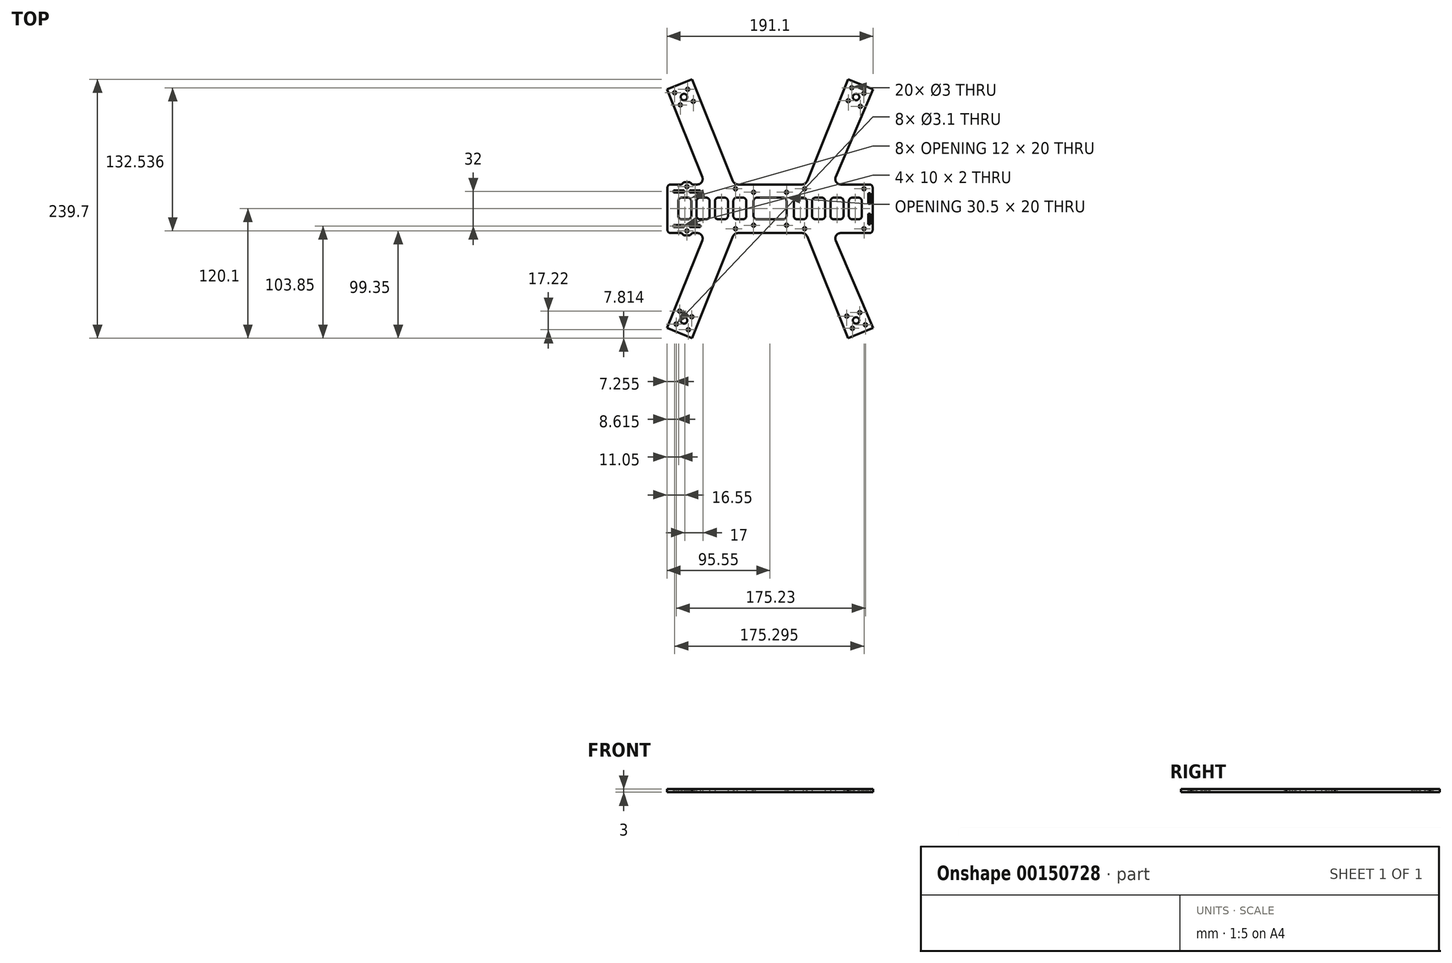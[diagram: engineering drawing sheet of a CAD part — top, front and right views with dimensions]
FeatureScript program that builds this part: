
annotation { "Feature Type Name" : "Feature", "Feature Type Description" : "" }
export const myFeature = defineFeature(function(context is Context, id is Id, definition is map)
    precondition{}
    {
        {
            var Q0;
            Q0=qCreatedBy(makeId("Top.planeOp"),FACE);
            var sketch = newSketch(context, id + "F0", { "sketchPlane" : qUnion([Q0])});
            skLineSegment(sketch, "E0.left", {"start": v(0, 42) * mm, "end": v(0, 3) * mm});
            skPoint(sketch, "E1.startSnap0", {"position": v(0, 22.5) * mm});
            skPoint(sketch, "E2.visualSharp", {"position": v(0, 45) * mm});
            skArc(sketch, "E2.filletArc", {"start": v(3, 45) * mm, "mid": v(0.88, 44.12) * mm, "end": v(0, 42) * mm});
            skPoint(sketch, "E3.visualSharp", {"position": v(0, 0) * mm});
            skArc(sketch, "E3.filletArc", {"start": v(0, 3) * mm, "mid": v(0.88, 0.88) * mm, "end": v(3, 0) * mm});
            skPoint(sketch, "E4.visualSharp", {"position": v(190, 45) * mm});
            skPoint(sketch, "E5.visualSharp", {"position": v(190, 0) * mm});
            skLineSegment(sketch, "E6", {"start": v(-0.55, -87.99) * mm, "end": v(22.63, -97.35) * mm});
            skLineSegment(sketch, "E7", {"start": v(95, 32.04) * mm, "end": v(95, 12.26) * mm, "construction": true});
            skPoint(sketch, "E7.startSnap0", {"position": v(95, 45) * mm});
            skLineSegment(sketch, "E8", {"start": v(11.04, -92.67) * mm, "end": v(15.32, -80.93) * mm, "construction": true});
            skCircle(sketch, "E9", {"center": v(15.32, -80.93) * mm, "radius": 13 * mm, "construction": true});
            skCircle(sketch, "E10", {"center": v(15.32, -80.93) * mm, "radius": 8 * mm, "construction": true});
            skCircle(sketch, "E11", {"center": v(15.32, -80.93) * mm, "radius": 9.5 * mm, "construction": true});
            skLineSegment(sketch, "E12", {"start": v(15.32, -80.93) * mm, "end": v(22.57, -77.54) * mm, "construction": true});
            skLineSegment(sketch, "E13", {"start": v(15.32, -80.93) * mm, "end": v(8.06, -84.3) * mm, "construction": true});
            skLineSegment(sketch, "E14", {"start": v(15.32, -80.93) * mm, "end": v(11.3, -72.32) * mm, "construction": true});
            skLineSegment(sketch, "E15", {"start": v(15.32, -80.93) * mm, "end": v(19.33, -89.54) * mm, "construction": true});
            skCircle(sketch, "E16", {"center": v(11.3, -72.32) * mm, "radius": 1.55 * mm});
            skCircle(sketch, "E17", {"center": v(19.33, -89.54) * mm, "radius": 1.55 * mm});
            skCircle(sketch, "E18", {"center": v(22.57, -77.54) * mm, "radius": 1.55 * mm});
            skCircle(sketch, "E19", {"center": v(8.06, -84.3) * mm, "radius": 1.55 * mm});
            skCircle(sketch, "E20", {"center": v(15.32, -80.93) * mm, "radius": 3 * mm});
            skLineSegment(sketch, "E21.MirrorCS", {"start": v(190.55, -87.99) * mm, "end": v(167.37, -97.35) * mm});
            skCircle(sketch, "E22.MirrorC", {"center": v(174.68, -80.93) * mm, "radius": 3 * mm});
            skLineSegment(sketch, "E23.MirrorCS", {"start": v(178.96, -92.67) * mm, "end": v(174.68, -80.93) * mm, "construction": true});
            skCircle(sketch, "E24.MirrorC", {"center": v(174.68, -80.93) * mm, "radius": 8 * mm, "construction": true});
            skCircle(sketch, "E25.MirrorC", {"center": v(174.68, -80.93) * mm, "radius": 9.5 * mm, "construction": true});
            skLineSegment(sketch, "E26", {"start": v(174.68, -80.93) * mm, "end": v(166.07, -76.91) * mm, "construction": true});
            skLineSegment(sketch, "E27", {"start": v(174.68, -80.93) * mm, "end": v(183.3, -84.94) * mm, "construction": true});
            skLineSegment(sketch, "E28", {"start": v(174.68, -80.93) * mm, "end": v(178.07, -73.68) * mm, "construction": true});
            skLineSegment(sketch, "E29", {"start": v(174.68, -80.93) * mm, "end": v(171.3, -88.18) * mm, "construction": true});
            skCircle(sketch, "E30", {"center": v(166.07, -76.91) * mm, "radius": 1.55 * mm});
            skCircle(sketch, "E31", {"center": v(178.07, -73.68) * mm, "radius": 1.55 * mm});
            skCircle(sketch, "E32", {"center": v(171.3, -88.18) * mm, "radius": 1.55 * mm});
            skCircle(sketch, "E33", {"center": v(183.3, -84.94) * mm, "radius": 1.55 * mm});
            skLineSegment(sketch, "E34.bottom", {"start": v(110.25, 7.25) * mm, "end": v(79.75, 7.25) * mm, "construction": true});
            skLineSegment(sketch, "E34.top", {"start": v(110.25, 37.75) * mm, "end": v(79.75, 37.75) * mm, "construction": true});
            skCircle(sketch, "E35", {"center": v(110.25, 7.25) * mm, "radius": 1.5 * mm});
            skCircle(sketch, "E36", {"center": v(79.75, 7.25) * mm, "radius": 1.5 * mm});
            skCircle(sketch, "E37", {"center": v(110.25, 37.75) * mm, "radius": 1.5 * mm});
            skCircle(sketch, "E38", {"center": v(79.75, 37.75) * mm, "radius": 1.5 * mm});
            skLineSegment(sketch, "E39.bottom", {"start": v(177, 12.75) * mm, "end": v(171, 12.75) * mm});
            skLineSegment(sketch, "E39.top", {"start": v(177, 32.75) * mm, "end": v(171, 32.75) * mm});
            skLineSegment(sketch, "E39.left", {"start": v(180, 15.75) * mm, "end": v(180, 29.75) * mm});
            skLineSegment(sketch, "E39.right", {"start": v(168, 15.75) * mm, "end": v(168, 29.75) * mm});
            skPoint(sketch, "E40.visualSharp", {"position": v(180, 12.75) * mm});
            skArc(sketch, "E40.filletArc", {"start": v(177, 12.75) * mm, "mid": v(179.12, 13.63) * mm, "end": v(180, 15.75) * mm});
            skPoint(sketch, "E41.visualSharp", {"position": v(168, 12.75) * mm});
            skArc(sketch, "E41.filletArc", {"start": v(168, 15.75) * mm, "mid": v(168.88, 13.63) * mm, "end": v(171, 12.75) * mm});
            skPoint(sketch, "E42.visualSharp", {"position": v(168, 32.75) * mm});
            skArc(sketch, "E42.filletArc", {"start": v(171, 32.75) * mm, "mid": v(168.88, 31.87) * mm, "end": v(168, 29.75) * mm});
            skPoint(sketch, "E43.visualSharp", {"position": v(180, 32.75) * mm});
            skArc(sketch, "E43.filletArc", {"start": v(180, 29.75) * mm, "mid": v(179.12, 31.87) * mm, "end": v(177, 32.75) * mm});
            skPoint(sketch, "E44.1.0.0", {"position": v(163, 12.75) * mm});
            skLineSegment(sketch, "E44.1.0.1", {"start": v(151, 15.75) * mm, "end": v(151, 29.75) * mm});
            skLineSegment(sketch, "E44.1.0.2", {"start": v(160, 32.75) * mm, "end": v(154, 32.75) * mm});
            skLineSegment(sketch, "E44.1.0.3", {"start": v(163, 15.75) * mm, "end": v(163, 29.75) * mm});
            skLineSegment(sketch, "E44.1.0.4", {"start": v(160, 12.75) * mm, "end": v(154, 12.75) * mm});
            skPoint(sketch, "E44.1.0.5", {"position": v(151, 12.75) * mm});
            skPoint(sketch, "E44.1.0.6", {"position": v(163, 32.75) * mm});
            skPoint(sketch, "E44.1.0.7", {"position": v(151, 32.75) * mm});
            skArc(sketch, "E44.1.0.8", {"start": v(160, 12.75) * mm, "mid": v(162.12, 13.63) * mm, "end": v(163, 15.75) * mm});
            skArc(sketch, "E44.1.0.9", {"start": v(154, 32.75) * mm, "mid": v(151.88, 31.87) * mm, "end": v(151, 29.75) * mm});
            skArc(sketch, "E44.1.0.10", {"start": v(151, 15.75) * mm, "mid": v(151.88, 13.63) * mm, "end": v(154, 12.75) * mm});
            skArc(sketch, "E44.1.0.11", {"start": v(163, 29.75) * mm, "mid": v(162.12, 31.87) * mm, "end": v(160, 32.75) * mm});
            skPoint(sketch, "E44.2.0.0", {"position": v(146, 12.75) * mm});
            skLineSegment(sketch, "E44.2.0.1", {"start": v(134, 15.75) * mm, "end": v(134, 29.75) * mm});
            skLineSegment(sketch, "E44.2.0.2", {"start": v(143, 32.75) * mm, "end": v(137, 32.75) * mm});
            skLineSegment(sketch, "E44.2.0.3", {"start": v(146, 15.75) * mm, "end": v(146, 29.75) * mm});
            skLineSegment(sketch, "E44.2.0.4", {"start": v(143, 12.75) * mm, "end": v(137, 12.75) * mm});
            skPoint(sketch, "E44.2.0.5", {"position": v(134, 12.75) * mm});
            skPoint(sketch, "E44.2.0.6", {"position": v(146, 32.75) * mm});
            skPoint(sketch, "E44.2.0.7", {"position": v(134, 32.75) * mm});
            skArc(sketch, "E44.2.0.8", {"start": v(143, 12.75) * mm, "mid": v(145.12, 13.63) * mm, "end": v(146, 15.75) * mm});
            skArc(sketch, "E44.2.0.9", {"start": v(137, 32.75) * mm, "mid": v(134.88, 31.87) * mm, "end": v(134, 29.75) * mm});
            skArc(sketch, "E44.2.0.10", {"start": v(134, 15.75) * mm, "mid": v(134.88, 13.63) * mm, "end": v(137, 12.75) * mm});
            skArc(sketch, "E44.2.0.11", {"start": v(146, 29.75) * mm, "mid": v(145.12, 31.87) * mm, "end": v(143, 32.75) * mm});
            skPoint(sketch, "E44.3.0.0", {"position": v(129, 12.75) * mm});
            skLineSegment(sketch, "E44.3.0.1", {"start": v(117, 15.75) * mm, "end": v(117, 29.75) * mm});
            skLineSegment(sketch, "E44.3.0.2", {"start": v(126, 32.75) * mm, "end": v(120, 32.75) * mm});
            skLineSegment(sketch, "E44.3.0.3", {"start": v(129, 15.75) * mm, "end": v(129, 29.75) * mm});
            skLineSegment(sketch, "E44.3.0.4", {"start": v(126, 12.75) * mm, "end": v(120, 12.75) * mm});
            skPoint(sketch, "E44.3.0.5", {"position": v(117, 12.75) * mm});
            skPoint(sketch, "E44.3.0.6", {"position": v(129, 32.75) * mm});
            skPoint(sketch, "E44.3.0.7", {"position": v(117, 32.75) * mm});
            skArc(sketch, "E44.3.0.8", {"start": v(126, 12.75) * mm, "mid": v(128.12, 13.63) * mm, "end": v(129, 15.75) * mm});
            skArc(sketch, "E44.3.0.9", {"start": v(120, 32.75) * mm, "mid": v(117.88, 31.87) * mm, "end": v(117, 29.75) * mm});
            skArc(sketch, "E44.3.0.10", {"start": v(117, 15.75) * mm, "mid": v(117.88, 13.63) * mm, "end": v(120, 12.75) * mm});
            skArc(sketch, "E44.3.0.11", {"start": v(129, 29.75) * mm, "mid": v(128.12, 31.87) * mm, "end": v(126, 32.75) * mm});
            skLineSegment(sketch, "E44.direction1", {"start": v(168, 12.75) * mm, "end": v(151, 12.75) * mm, "construction": true});
            skLineSegment(sketch, "E45.bottom", {"start": v(107.25, 12.75) * mm, "end": v(82.75, 12.75) * mm});
            skLineSegment(sketch, "E45.top", {"start": v(107.25, 32.75) * mm, "end": v(82.75, 32.75) * mm});
            skLineSegment(sketch, "E45.left", {"start": v(110.25, 15.75) * mm, "end": v(110.25, 29.75) * mm});
            skLineSegment(sketch, "E45.right", {"start": v(79.75, 15.75) * mm, "end": v(79.75, 29.75) * mm});
            skPoint(sketch, "E46.visualSharp", {"position": v(110.25, 12.75) * mm});
            skArc(sketch, "E46.filletArc", {"start": v(107.25, 12.75) * mm, "mid": v(109.37, 13.63) * mm, "end": v(110.25, 15.75) * mm});
            skPoint(sketch, "E47.visualSharp", {"position": v(110.25, 32.75) * mm});
            skArc(sketch, "E47.filletArc", {"start": v(110.25, 29.75) * mm, "mid": v(109.37, 31.87) * mm, "end": v(107.25, 32.75) * mm});
            skPoint(sketch, "E48.visualSharp", {"position": v(79.75, 32.75) * mm});
            skArc(sketch, "E48.filletArc", {"start": v(82.75, 32.75) * mm, "mid": v(80.63, 31.87) * mm, "end": v(79.75, 29.75) * mm});
            skPoint(sketch, "E49.visualSharp", {"position": v(79.75, 12.75) * mm});
            skArc(sketch, "E49.filletArc", {"start": v(79.75, 15.75) * mm, "mid": v(80.63, 13.63) * mm, "end": v(82.75, 12.75) * mm});
            skArc(sketch, "E50.MirrorCS", {"start": v(44, 29.75) * mm, "mid": v(44.88, 31.87) * mm, "end": v(47, 32.75) * mm});
            skArc(sketch, "E51.MirrorCS", {"start": v(61, 29.75) * mm, "mid": v(61.88, 31.87) * mm, "end": v(64, 32.75) * mm});
            skArc(sketch, "E52.MirrorCS", {"start": v(70, 32.75) * mm, "mid": v(72.12, 31.87) * mm, "end": v(73, 29.75) * mm});
            skArc(sketch, "E53.MirrorCS", {"start": v(64, 12.75) * mm, "mid": v(61.88, 13.63) * mm, "end": v(61, 15.75) * mm});
            skArc(sketch, "E54.MirrorCS", {"start": v(73, 15.75) * mm, "mid": v(72.12, 13.63) * mm, "end": v(70, 12.75) * mm});
            skArc(sketch, "E55.MirrorCS", {"start": v(53, 32.75) * mm, "mid": v(55.12, 31.87) * mm, "end": v(56, 29.75) * mm});
            skArc(sketch, "E56.MirrorCS", {"start": v(56, 15.75) * mm, "mid": v(55.12, 13.63) * mm, "end": v(53, 12.75) * mm});
            skArc(sketch, "E57.MirrorCS", {"start": v(47, 12.75) * mm, "mid": v(44.88, 13.63) * mm, "end": v(44, 15.75) * mm});
            skLineSegment(sketch, "E58.MirrorCS", {"start": v(56, 15.75) * mm, "end": v(56, 29.75) * mm});
            skPoint(sketch, "E59.MirrorP", {"position": v(44, 12.75) * mm});
            skLineSegment(sketch, "E60.MirrorCS", {"start": v(64, 32.75) * mm, "end": v(70, 32.75) * mm});
            skPoint(sketch, "E61.MirrorP", {"position": v(61, 12.75) * mm});
            skPoint(sketch, "E62.MirrorP", {"position": v(39, 12.75) * mm});
            skPoint(sketch, "E63.MirrorP", {"position": v(44, 32.75) * mm});
            skPoint(sketch, "E64.MirrorP", {"position": v(56, 12.75) * mm});
            skLineSegment(sketch, "E65.MirrorCS", {"start": v(44, 15.75) * mm, "end": v(44, 29.75) * mm});
            skLineSegment(sketch, "E66.MirrorCS", {"start": v(47, 12.75) * mm, "end": v(53, 12.75) * mm});
            skLineSegment(sketch, "E67.MirrorCS", {"start": v(73, 15.75) * mm, "end": v(73, 29.75) * mm});
            skPoint(sketch, "E68.MirrorP", {"position": v(73, 32.75) * mm});
            skPoint(sketch, "E69.MirrorP", {"position": v(61, 32.75) * mm});
            skLineSegment(sketch, "E70.MirrorCS", {"start": v(64, 12.75) * mm, "end": v(70, 12.75) * mm});
            skLineSegment(sketch, "E71.MirrorCS", {"start": v(47, 32.75) * mm, "end": v(53, 32.75) * mm});
            skPoint(sketch, "E72.MirrorP", {"position": v(73, 12.75) * mm});
            skPoint(sketch, "E73.MirrorP", {"position": v(39, 32.75) * mm});
            skPoint(sketch, "E74.MirrorP", {"position": v(56, 32.75) * mm});
            skLineSegment(sketch, "E75.MirrorCS", {"start": v(61, 15.75) * mm, "end": v(61, 29.75) * mm});
            skLineSegment(sketch, "E76.bottom", {"start": v(20.5, 39.5) * mm, "end": v(30.5, 39.5) * mm});
            skLineSegment(sketch, "E76.top", {"start": v(20.5, 37.5) * mm, "end": v(30.5, 37.5) * mm});
            skLineSegment(sketch, "E76.left", {"start": v(20.5, 39.5) * mm, "end": v(20.5, 37.5) * mm});
            skLineSegment(sketch, "E76.right", {"start": v(30.5, 39.5) * mm, "end": v(30.5, 37.5) * mm});
            skLineSegment(sketch, "E77.MirrorCS", {"start": v(30.5, 5.5) * mm, "end": v(30.5, 7.5) * mm});
            skLineSegment(sketch, "E78.MirrorCS", {"start": v(20.5, 5.5) * mm, "end": v(20.5, 7.5) * mm});
            skLineSegment(sketch, "E79.MirrorCS", {"start": v(15.5, 5.5) * mm, "end": v(15.5, 7.5) * mm});
            skLineSegment(sketch, "E80.MirrorCS", {"start": v(5.5, 5.5) * mm, "end": v(5.5, 7.5) * mm});
            skLineSegment(sketch, "E81.MirrorCS", {"start": v(20.5, 7.5) * mm, "end": v(30.5, 7.5) * mm});
            skLineSegment(sketch, "E82.MirrorCS", {"start": v(20.5, 5.5) * mm, "end": v(30.5, 5.5) * mm});
            skLineSegment(sketch, "E83.MirrorCS", {"start": v(5.5, 7.5) * mm, "end": v(15.5, 7.5) * mm});
            skLineSegment(sketch, "E84.MirrorCS", {"start": v(5.5, 5.5) * mm, "end": v(15.5, 5.5) * mm});
            skLineSegment(sketch, "E85", {"start": v(87.1, 22.5) * mm, "end": v(104.02, 22.5) * mm, "construction": true});
            skCircle(sketch, "E86", {"center": v(63, 41) * mm, "radius": 1.5 * mm});
            skCircle(sketch, "E87.MirrorC", {"center": v(63, 4) * mm, "radius": 1.5 * mm});
            skLineSegment(sketch, "E88.bottom", {"start": v(186, 37) * mm, "end": v(188, 37) * mm});
            skLineSegment(sketch, "E88.top", {"start": v(186, 27) * mm, "end": v(188, 27) * mm});
            skLineSegment(sketch, "E88.left", {"start": v(186, 37) * mm, "end": v(186, 27) * mm});
            skLineSegment(sketch, "E88.right", {"start": v(188, 37) * mm, "end": v(188, 27) * mm});
            skLineSegment(sketch, "E89.MirrorCS", {"start": v(188, 8) * mm, "end": v(188, 18) * mm});
            skLineSegment(sketch, "E90.MirrorCS", {"start": v(186, 8) * mm, "end": v(186, 18) * mm});
            skLineSegment(sketch, "E91.MirrorCS", {"start": v(186, 18) * mm, "end": v(188, 18) * mm});
            skLineSegment(sketch, "E92.MirrorCS", {"start": v(186, 8) * mm, "end": v(188, 8) * mm});
            skCircle(sketch, "E93", {"center": v(182, 41) * mm, "radius": 1.5 * mm});
            skCircle(sketch, "E94.MirrorC", {"center": v(182, 4) * mm, "radius": 1.5 * mm});
            skCircle(sketch, "E95", {"center": v(127, 41) * mm, "radius": 1.5 * mm});
            skCircle(sketch, "E96.MirrorC", {"center": v(127, 4) * mm, "radius": 1.5 * mm});
            skLineSegment(sketch, "E97.MirrorCS", {"start": v(5.5, 39.5) * mm, "end": v(5.5, 37.5) * mm});
            skLineSegment(sketch, "E98.MirrorCS", {"start": v(15.5, 39.5) * mm, "end": v(15.5, 37.5) * mm});
            skLineSegment(sketch, "E99.MirrorCS", {"start": v(5.5, 37.5) * mm, "end": v(15.5, 37.5) * mm});
            skLineSegment(sketch, "E100.MirrorCS", {"start": v(5.5, 39.5) * mm, "end": v(15.5, 39.5) * mm});
            skLineSegment(sketch, "E101", {"start": v(13, 45) * mm, "end": v(14.7, 46.7) * mm});
            skLineSegment(sketch, "E102", {"start": v(15.41, 47) * mm, "end": v(20.59, 47) * mm});
            skLineSegment(sketch, "E103", {"start": v(21.3, 46.7) * mm, "end": v(23, 45) * mm});
            skPoint(sketch, "E104.visualSharp", {"position": v(15, 47) * mm});
            skArc(sketch, "E104.filletArc", {"start": v(15.41, 47) * mm, "mid": v(15.03, 46.92) * mm, "end": v(14.7, 46.7) * mm});
            skPoint(sketch, "E105.visualSharp", {"position": v(21, 47) * mm});
            skArc(sketch, "E105.filletArc", {"start": v(21.3, 46.7) * mm, "mid": v(20.97, 46.92) * mm, "end": v(20.59, 47) * mm});
            skArc(sketch, "E106.MirrorCS", {"start": v(39, 15.75) * mm, "mid": v(38.12, 13.63) * mm, "end": v(36, 12.75) * mm});
            skArc(sketch, "E107.MirrorCS", {"start": v(22, 15.75) * mm, "mid": v(21.12, 13.63) * mm, "end": v(19, 12.75) * mm});
            skArc(sketch, "E108.MirrorCS", {"start": v(36, 32.75) * mm, "mid": v(38.12, 31.87) * mm, "end": v(39, 29.75) * mm});
            skArc(sketch, "E109.MirrorCS", {"start": v(30, 12.75) * mm, "mid": v(27.88, 13.63) * mm, "end": v(27, 15.75) * mm});
            skLineSegment(sketch, "E110.MirrorCS", {"start": v(30, 12.75) * mm, "end": v(36, 12.75) * mm});
            skArc(sketch, "E111.MirrorCS", {"start": v(10, 29.75) * mm, "mid": v(10.88, 31.87) * mm, "end": v(13, 32.75) * mm});
            skArc(sketch, "E112.MirrorCS", {"start": v(19, 32.75) * mm, "mid": v(21.12, 31.87) * mm, "end": v(22, 29.75) * mm});
            skArc(sketch, "E113.MirrorCS", {"start": v(13, 12.75) * mm, "mid": v(10.88, 13.63) * mm, "end": v(10, 15.75) * mm});
            skArc(sketch, "E114.MirrorCS", {"start": v(27, 29.75) * mm, "mid": v(27.88, 31.87) * mm, "end": v(30, 32.75) * mm});
            skPoint(sketch, "E115.MirrorP", {"position": v(27, 12.75) * mm});
            skPoint(sketch, "E116.MirrorP", {"position": v(10, 32.75) * mm});
            skLineSegment(sketch, "E117.MirrorCS", {"start": v(30, 32.75) * mm, "end": v(36, 32.75) * mm});
            skPoint(sketch, "E118.MirrorP", {"position": v(22, 12.75) * mm});
            skLineSegment(sketch, "E119.MirrorCS", {"start": v(27, 15.75) * mm, "end": v(27, 29.75) * mm});
            skPoint(sketch, "E120.MirrorP", {"position": v(22, 32.75) * mm});
            skLineSegment(sketch, "E121.MirrorCS", {"start": v(39, 15.75) * mm, "end": v(39, 29.75) * mm});
            skPoint(sketch, "E122.MirrorP", {"position": v(10, 12.75) * mm});
            skPoint(sketch, "E123.MirrorP", {"position": v(27, 32.75) * mm});
            skLineSegment(sketch, "E124.MirrorCS", {"start": v(22, 15.75) * mm, "end": v(22, 29.75) * mm});
            skLineSegment(sketch, "E125.MirrorCS", {"start": v(10, 15.75) * mm, "end": v(10, 29.75) * mm});
            skLineSegment(sketch, "E126.MirrorCS", {"start": v(13, 32.75) * mm, "end": v(19, 32.75) * mm});
            skLineSegment(sketch, "E127.MirrorCS", {"start": v(22, 12.75) * mm, "end": v(39, 12.75) * mm, "construction": true});
            skLineSegment(sketch, "E128.MirrorCS", {"start": v(13, 12.75) * mm, "end": v(19, 12.75) * mm});
            skCircle(sketch, "E129", {"center": v(18, 43) * mm, "radius": 1.5 * mm});
            skCircle(sketch, "E130.MirrorC", {"center": v(18, 2) * mm, "radius": 1.5 * mm});
            skArc(sketch, "E131.MirrorCS", {"start": v(21.3, -1.7) * mm, "mid": v(20.97, -1.92) * mm, "end": v(20.59, -2) * mm});
            skArc(sketch, "E132.MirrorCS", {"start": v(15.41, -2) * mm, "mid": v(15.03, -1.92) * mm, "end": v(14.7, -1.7) * mm});
            skPoint(sketch, "E133.MirrorP", {"position": v(21, -2) * mm});
            skLineSegment(sketch, "E134.MirrorCS", {"start": v(15.41, -2) * mm, "end": v(20.59, -2) * mm});
            skPoint(sketch, "E135.MirrorP", {"position": v(15, -2) * mm});
            skLineSegment(sketch, "E136.MirrorCS", {"start": v(13, 0) * mm, "end": v(14.7, -1.7) * mm});
            skLineSegment(sketch, "E137.MirrorCS", {"start": v(21.3, -1.7) * mm, "end": v(23, 0) * mm});
            skCircle(sketch, "E138", {"center": v(15.32, -80.93) * mm, "radius": 77 * mm, "construction": true});
            skLineSegment(sketch, "E139", {"start": v(13, 0) * mm, "end": v(3, 0) * mm});
            skCircle(sketch, "E140.MirrorC", {"center": v(174.68, -80.93) * mm, "radius": 77 * mm, "construction": true});
            skPoint(sketch, "E141.visualSharp", {"position": v(61.96, 0) * mm});
            skLineSegment(sketch, "E142.MirrorCS", {"start": v(167.37, -97.35) * mm, "end": v(129.3, -3.13) * mm});
            skLineSegment(sketch, "E143.MirrorCS", {"start": v(190.55, -87.99) * mm, "end": v(155.83, -6.97) * mm});
            skLineSegment(sketch, "E144", {"start": v(65.34, 0) * mm, "end": v(124.66, 0) * mm});
            skPoint(sketch, "E145.visualSharp", {"position": v(128.04, 0) * mm});
            skArc(sketch, "E145.filletArc", {"start": v(129.3, -3.13) * mm, "mid": v(127.46, -0.85) * mm, "end": v(124.66, 0) * mm});
            skPoint(sketch, "E146.visualSharp", {"position": v(152.85, 0) * mm});
            skArc(sketch, "E146.filletArc", {"start": v(160.43, 0) * mm, "mid": v(156.26, -2.25) * mm, "end": v(155.83, -6.97) * mm});
            skLineSegment(sketch, "E147.MirrorCS", {"start": v(13, 45) * mm, "end": v(3, 45) * mm});
            skCircle(sketch, "E148.MirrorC", {"center": v(15.32, 125.93) * mm, "radius": 77 * mm, "construction": true});
            skArc(sketch, "E149.MirrorCS", {"start": v(129.3, 48.13) * mm, "mid": v(127.46, 45.85) * mm, "end": v(124.66, 45) * mm});
            skLineSegment(sketch, "E150.MirrorCS", {"start": v(190.55, 132.99) * mm, "end": v(155.83, 51.97) * mm});
            skLineSegment(sketch, "E151.MirrorCS", {"start": v(190.55, 132.99) * mm, "end": v(167.37, 142.35) * mm});
            skCircle(sketch, "E152.MirrorC", {"center": v(174.68, 125.93) * mm, "radius": 77 * mm, "construction": true});
            skLineSegment(sketch, "E153.MirrorCS", {"start": v(-0.55, 132.99) * mm, "end": v(22.63, 142.35) * mm});
            skCircle(sketch, "E154.MirrorC", {"center": v(15.32, 125.93) * mm, "radius": 9.5 * mm, "construction": true});
            skCircle(sketch, "E155.MirrorC", {"center": v(15.32, 125.93) * mm, "radius": 8 * mm, "construction": true});
            skCircle(sketch, "E156.MirrorC", {"center": v(15.32, 125.93) * mm, "radius": 3 * mm});
            skCircle(sketch, "E157.MirrorC", {"center": v(174.68, 125.93) * mm, "radius": 3 * mm});
            skCircle(sketch, "E158.MirrorC", {"center": v(174.68, 125.93) * mm, "radius": 8 * mm, "construction": true});
            skCircle(sketch, "E159.MirrorC", {"center": v(174.68, 125.93) * mm, "radius": 9.5 * mm, "construction": true});
            skLineSegment(sketch, "E160", {"start": v(174.68, 125.93) * mm, "end": v(167.43, 122.54) * mm, "construction": true});
            skLineSegment(sketch, "E161", {"start": v(174.68, 125.93) * mm, "end": v(170.67, 134.54) * mm, "construction": true});
            skLineSegment(sketch, "E162", {"start": v(174.68, 125.93) * mm, "end": v(178.7, 117.32) * mm, "construction": true});
            skLineSegment(sketch, "E163", {"start": v(174.68, 125.93) * mm, "end": v(181.94, 129.3) * mm});
            skLineSegment(sketch, "E164", {"start": v(15.32, 125.93) * mm, "end": v(6.7, 129.94) * mm, "construction": true});
            skLineSegment(sketch, "E165", {"start": v(15.32, 125.93) * mm, "end": v(23.93, 121.91) * mm, "construction": true});
            skLineSegment(sketch, "E166", {"start": v(15.32, 125.93) * mm, "end": v(11.93, 118.68) * mm, "construction": true});
            skLineSegment(sketch, "E167", {"start": v(15.32, 125.93) * mm, "end": v(18.7, 133.18) * mm, "construction": true});
            skCircle(sketch, "E168", {"center": v(6.7, 129.94) * mm, "radius": 1.5 * mm});
            skCircle(sketch, "E169", {"center": v(18.7, 133.18) * mm, "radius": 1.5 * mm});
            skCircle(sketch, "E170", {"center": v(23.93, 121.91) * mm, "radius": 1.5 * mm});
            skCircle(sketch, "E171", {"center": v(11.93, 118.68) * mm, "radius": 1.5 * mm});
            skCircle(sketch, "E172", {"center": v(170.67, 134.54) * mm, "radius": 1.5 * mm});
            skCircle(sketch, "E173", {"center": v(181.94, 129.3) * mm, "radius": 1.5 * mm});
            skCircle(sketch, "E174", {"center": v(178.7, 117.32) * mm, "radius": 1.5 * mm});
            skCircle(sketch, "E175", {"center": v(167.43, 122.54) * mm, "radius": 1.5 * mm});
            skLineSegment(sketch, "E176", {"start": v(22.63, -97.35) * mm, "end": v(60.7, -3.13) * mm});
            skLineSegment(sketch, "E177", {"start": v(-0.55, -87.99) * mm, "end": v(32.22, -6.87) * mm});
            skLineSegment(sketch, "E178", {"start": v(23, 0) * mm, "end": v(27.59, 0) * mm});
            skLineSegment(sketch, "E179.MirrorCS", {"start": v(23, 45) * mm, "end": v(27.59, 45) * mm});
            skLineSegment(sketch, "E180.MirrorCS", {"start": v(-0.55, 132.99) * mm, "end": v(32.22, 51.87) * mm});
            skLineSegment(sketch, "E181.MirrorCS", {"start": v(22.63, 142.35) * mm, "end": v(60.7, 48.13) * mm});
            skLineSegment(sketch, "E182.MirrorCS", {"start": v(65.34, 45) * mm, "end": v(124.66, 45) * mm});
            skLineSegment(sketch, "E183.MirrorCS", {"start": v(167.37, 142.35) * mm, "end": v(129.3, 48.13) * mm});
            skArc(sketch, "E184.MirrorCS", {"start": v(160.43, 45) * mm, "mid": v(156.26, 47.25) * mm, "end": v(155.83, 51.97) * mm});
            skLineSegment(sketch, "E185", {"start": v(160.43, 0) * mm, "end": v(187, 0) * mm});
            skLineSegment(sketch, "E186", {"start": v(190, 3) * mm, "end": v(190, 42) * mm});
            skLineSegment(sketch, "E187", {"start": v(187, 45) * mm, "end": v(160.43, 45) * mm});
            skArc(sketch, "E188.filletArc", {"start": v(187, 0) * mm, "mid": v(189.12, 0.88) * mm, "end": v(190, 3) * mm});
            skArc(sketch, "E189.filletArc", {"start": v(190, 42) * mm, "mid": v(189.12, 44.12) * mm, "end": v(187, 45) * mm});
            skArc(sketch, "E190.filletArc", {"start": v(65.34, 0) * mm, "mid": v(62.54, -0.85) * mm, "end": v(60.7, -3.13) * mm});
            skPoint(sketch, "E191.visualSharp", {"position": v(35, 0) * mm});
            skArc(sketch, "E191.filletArc", {"start": v(32.22, -6.87) * mm, "mid": v(31.73, -2.2) * mm, "end": v(27.59, 0) * mm});
            skPoint(sketch, "E192.visualSharp", {"position": v(35, 45) * mm});
            skArc(sketch, "E192.filletArc", {"start": v(27.59, 45) * mm, "mid": v(31.73, 47.2) * mm, "end": v(32.22, 51.87) * mm});
            skPoint(sketch, "E193.visualSharp", {"position": v(61.96, 45) * mm});
            skArc(sketch, "E193.filletArc", {"start": v(60.7, 48.13) * mm, "mid": v(62.54, 45.85) * mm, "end": v(65.34, 45) * mm});
            skSolve(sketch);
        }
        {
            var Q0;
            Q0=makeQuery(id+"F0.imprint","IMPRINT",FACE,{"disambiguationData":[TD([[makeQuery(id+"F0.imprint","IMPRINT",EDGE,{"derivedFrom":sQuery(id+"F0.wireOp",EDGE,"E0.left")}),1.0]])]});
            var Q1;
            Q1=makeQuery(id+"F0.imprint","IMPRINT",FACE,{"disambiguationData":[TD([[makeQuery(id+"F0.imprint","IMPRINT",EDGE,{"derivedFrom":sQuery(id+"F0.wireOp",EDGE,"E131.MirrorCS")}),-1.0]])]});
            var Q2;
            {var subQ1=sQuery(id+"F0.wireOp",EDGE,"E101");Q2=makeQuery(id+"F0.imprint","IMPRINT",FACE,{"disambiguationData":[TD([[makeQuery(id+"F0.imprint","IMPRINT",EDGE,{"derivedFrom":subQ1}),-1.0]])]});}
            extrude(context, id + "F1", {"entities" : qUnion([Q0, Q1, Q2]), "depth" : 3 * mm});
        }
    });
